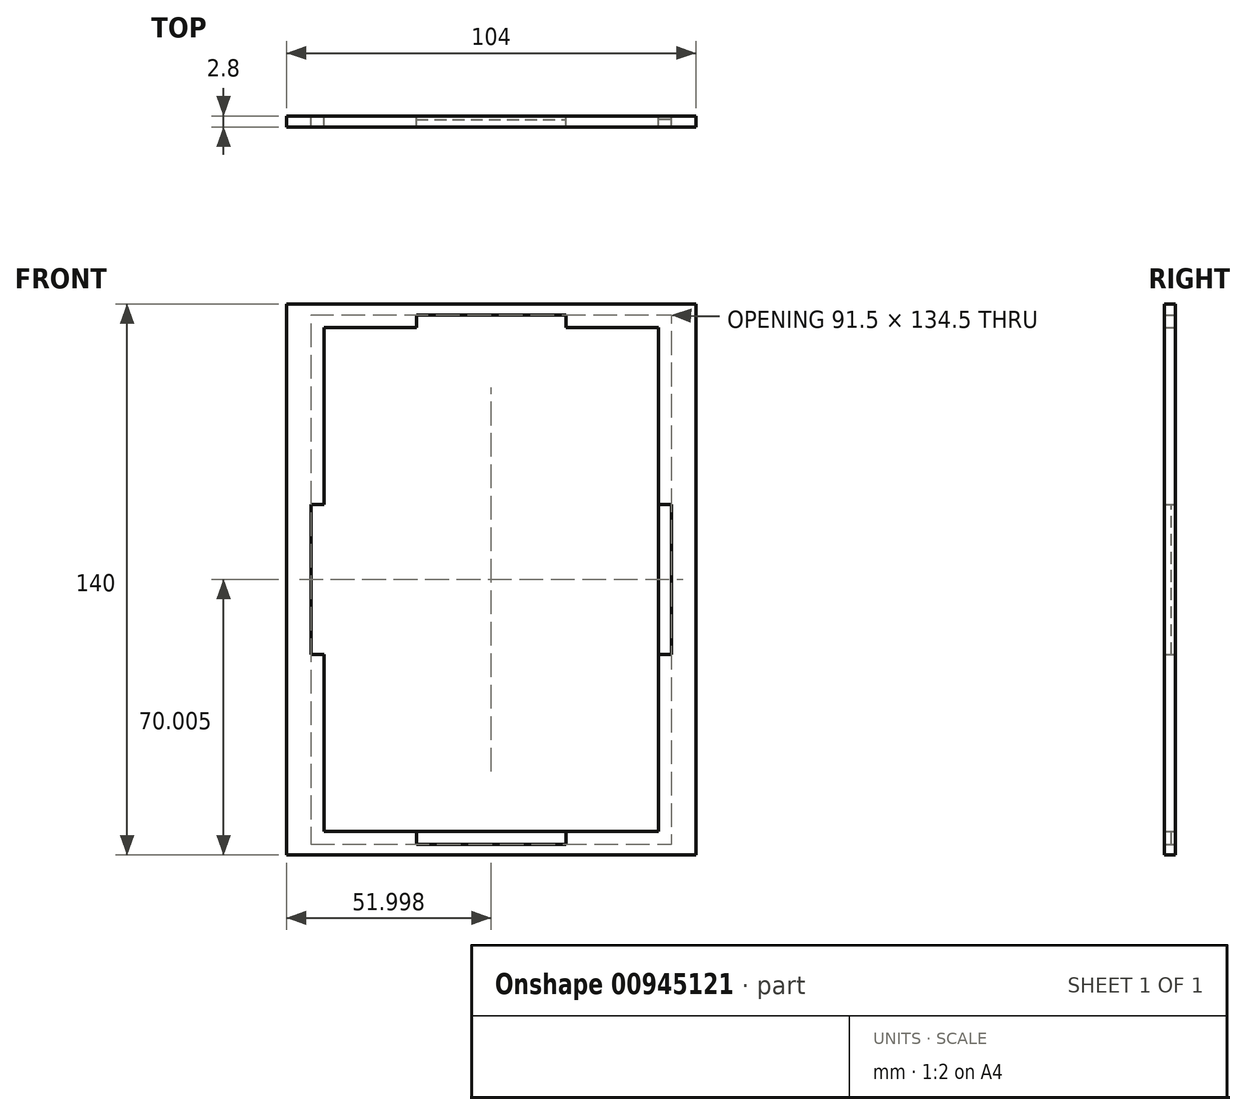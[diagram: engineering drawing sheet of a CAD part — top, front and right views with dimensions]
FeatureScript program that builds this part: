
annotation { "Feature Type Name" : "Feature", "Feature Type Description" : "" }
export const myFeature = defineFeature(function(context is Context, id is Id, definition is map)
    precondition{}
    {
        {
            var Q0;
            Q0=qCreatedBy(makeId("Front.planeOp"),FACE);
            var sketch = newSketch(context, id + "F0", { "sketchPlane" : qUnion([Q0])});
            skLineSegment(sketch, "E0.bottom", {"start": v(37.8, -54.45) * mm, "end": v(-66.2, -54.45) * mm});
            skLineSegment(sketch, "E0.top", {"start": v(37.8, 85.55) * mm, "end": v(-66.2, 85.55) * mm});
            skLineSegment(sketch, "E0.left", {"start": v(37.8, -54.45) * mm, "end": v(37.8, 85.55) * mm});
            skLineSegment(sketch, "E0.right", {"start": v(-66.2, -54.45) * mm, "end": v(-66.2, 85.55) * mm});
            skLineSegment(sketch, "E1", {"start": v(-14.2, 85.55) * mm, "end": v(-14.2, -54.45) * mm});
            skLineSegment(sketch, "E2", {"start": v(-66.2, 15.55) * mm, "end": v(37.8, 15.55) * mm});
            skLineSegment(sketch, "E3", {"start": v(-14.2, 15.55) * mm, "end": v(-56.7, 15.55) * mm});
            skLineSegment(sketch, "E4", {"start": v(-56.7, 15.55) * mm, "end": v(-56.7, 79.55) * mm});
            skLineSegment(sketch, "E5", {"start": v(-56.7, 79.55) * mm, "end": v(28.3, 79.55) * mm});
            skLineSegment(sketch, "E6.MirrorCS", {"start": v(28.3, 15.55) * mm, "end": v(28.3, 79.55) * mm});
            skLineSegment(sketch, "E7.MirrorCS", {"start": v(-56.7, -48.45) * mm, "end": v(28.3, -48.45) * mm});
            skLineSegment(sketch, "E8.MirrorCS", {"start": v(-56.7, 15.55) * mm, "end": v(-56.7, -48.45) * mm});
            skLineSegment(sketch, "E9.MirrorCS", {"start": v(28.3, 15.55) * mm, "end": v(28.3, -48.45) * mm});
            skLineSegment(sketch, "E10", {"start": v(-14.2, 79.55) * mm, "end": v(-14.2, 82.8) * mm});
            skLineSegment(sketch, "E11", {"start": v(-14.2, 82.8) * mm, "end": v(-33.2, 82.8) * mm});
            skLineSegment(sketch, "E12", {"start": v(-33.2, 82.8) * mm, "end": v(-33.2, 79.55) * mm});
            skLineSegment(sketch, "E13", {"start": v(-56.7, 15.55) * mm, "end": v(-59.95, 15.55) * mm});
            skLineSegment(sketch, "E14", {"start": v(-59.95, 15.55) * mm, "end": v(-59.95, -3.45) * mm});
            skLineSegment(sketch, "E15", {"start": v(-59.95, -3.45) * mm, "end": v(-59.95, 34.55) * mm});
            skLineSegment(sketch, "E16", {"start": v(-59.95, 34.55) * mm, "end": v(-56.7, 34.55) * mm});
            skLineSegment(sketch, "E17", {"start": v(-59.95, -3.45) * mm, "end": v(-56.7, -3.45) * mm});
            skLineSegment(sketch, "E18.MirrorCS", {"start": v(-14.2, 82.8) * mm, "end": v(4.8, 82.8) * mm});
            skLineSegment(sketch, "E19.MirrorCS", {"start": v(4.8, 82.8) * mm, "end": v(4.8, 79.55) * mm});
            skLineSegment(sketch, "E20.MirrorCS", {"start": v(31.55, 34.55) * mm, "end": v(28.3, 34.55) * mm});
            skLineSegment(sketch, "E21.MirrorCS", {"start": v(31.55, -3.45) * mm, "end": v(31.55, 34.55) * mm});
            skLineSegment(sketch, "E22.MirrorCS", {"start": v(31.55, -3.45) * mm, "end": v(28.3, -3.45) * mm});
            skLineSegment(sketch, "E23.MirrorCS", {"start": v(-14.2, -51.7) * mm, "end": v(-33.2, -51.7) * mm});
            skLineSegment(sketch, "E24.MirrorCS", {"start": v(-33.2, -51.7) * mm, "end": v(-33.2, -48.45) * mm});
            skLineSegment(sketch, "E25.MirrorCS", {"start": v(-14.2, -51.7) * mm, "end": v(4.8, -51.7) * mm});
            skLineSegment(sketch, "E26.MirrorCS", {"start": v(4.8, -51.7) * mm, "end": v(4.8, -48.45) * mm});
            skSolve(sketch);
        }
        {
            var Q0;
            {var subQ8=sQuery(id+"F0.wireOp",EDGE,"E11");Q0=makeQuery(id+"F0.imprint","IMPRINT",FACE,{"disambiguationData":[TD([[makeQuery(id+"F0.imprint","IMPRINT",EDGE,{"derivedFrom":subQ8}),-1.0]])]});}
            var Q1;
            {var subQ9=sQuery(id+"F0.wireOp",EDGE,"E18.MirrorCS");Q1=makeQuery(id+"F0.imprint","IMPRINT",FACE,{"disambiguationData":[TD([[makeQuery(id+"F0.imprint","IMPRINT",EDGE,{"derivedFrom":subQ9}),1.0]])]});}
            var Q2;
            {var subQ9=sQuery(id+"F0.wireOp",EDGE,"E22.MirrorCS");Q2=makeQuery(id+"F0.imprint","IMPRINT",FACE,{"disambiguationData":[TD([[makeQuery(id+"F0.imprint","IMPRINT",EDGE,{"derivedFrom":subQ9}),1.0]])]});}
            var Q3;
            {var subQ14=sQuery(id+"F0.wireOp",EDGE,"E17");Q3=makeQuery(id+"F0.imprint","IMPRINT",FACE,{"disambiguationData":[TD([[makeQuery(id+"F0.imprint","IMPRINT",EDGE,{"derivedFrom":subQ14}),-1.0]])]});}
            extrude(context, id + "F1", {"entities" : qUnion([Q0, Q1, Q2, Q3]), "depth" : 2.8 * mm, "offsetDistance" : 25 * mm});
        }
        {
            var Q0;
            {var subQ0=sQuery(id+"F0.wireOp",EDGE,"E13");Q0=makeQuery(id+"F0.imprint","IMPRINT",FACE,{"disambiguationData":[TD([[makeQuery(id+"F0.imprint","IMPRINT",EDGE,{"derivedFrom":subQ0}),-1.0]])]});}
            var Q1;
            {var subQ0=sQuery(id+"F0.wireOp",EDGE,"E13");Q1=makeQuery(id+"F0.imprint","IMPRINT",FACE,{"disambiguationData":[TD([[makeQuery(id+"F0.imprint","IMPRINT",EDGE,{"derivedFrom":subQ0}),1.0]])]});}
            var Q2;
            {var subQ0=sQuery(id+"F0.wireOp",EDGE,"E10");Q2=makeQuery(id+"F0.imprint","IMPRINT",FACE,{"disambiguationData":[TD([[makeQuery(id+"F0.imprint","IMPRINT",EDGE,{"derivedFrom":subQ0}),1.0]])]});}
            var Q3;
            {var subQ0=sQuery(id+"F0.wireOp",EDGE,"E10");Q3=makeQuery(id+"F0.imprint","IMPRINT",FACE,{"disambiguationData":[TD([[makeQuery(id+"F0.imprint","IMPRINT",EDGE,{"derivedFrom":subQ0}),-1.0]])]});}
            var Q4;
            {var subQ5=sQuery(id+"F0.wireOp",EDGE,"E20.MirrorCS");Q4=makeQuery(id+"F0.imprint","IMPRINT",FACE,{"disambiguationData":[TD([[makeQuery(id+"F0.imprint","IMPRINT",EDGE,{"derivedFrom":subQ5}),1.0]])]});}
            var Q5;
            {var subQ5=sQuery(id+"F0.wireOp",EDGE,"E22.MirrorCS");Q5=makeQuery(id+"F0.imprint","IMPRINT",FACE,{"disambiguationData":[TD([[makeQuery(id+"F0.imprint","IMPRINT",EDGE,{"derivedFrom":subQ5}),-1.0]])]});}
            var Q6;
            {var subQ0=sQuery(id+"F0.wireOp",EDGE,"E23.MirrorCS");Q6=makeQuery(id+"F0.imprint","IMPRINT",FACE,{"disambiguationData":[TD([[makeQuery(id+"F0.imprint","IMPRINT",EDGE,{"derivedFrom":subQ0}),-1.0]])]});}
            var Q7;
            {var subQ0=sQuery(id+"F0.wireOp",EDGE,"E25.MirrorCS");Q7=makeQuery(id+"F0.imprint","IMPRINT",FACE,{"disambiguationData":[TD([[makeQuery(id+"F0.imprint","IMPRINT",EDGE,{"derivedFrom":subQ0}),1.0]])]});}
            extrude(context, id + "F2", {"entities" : qUnion([Q0, Q1, Q2, Q3, Q4, Q5, Q6, Q7]), "depth" : 1 * mm, "offsetDistance" : 25 * mm});
        }
    });
